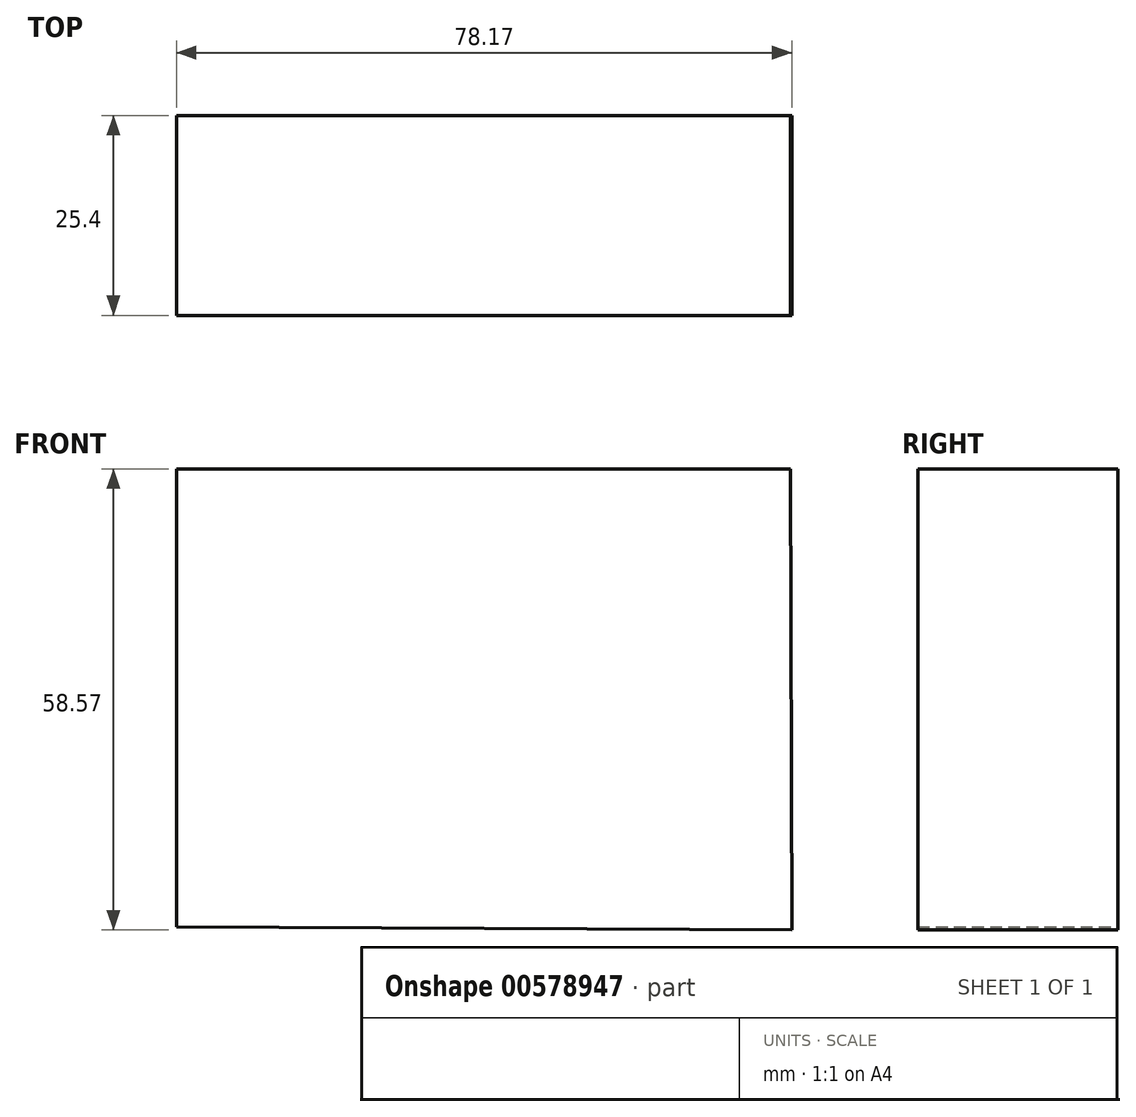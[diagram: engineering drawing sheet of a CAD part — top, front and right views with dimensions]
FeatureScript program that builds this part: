
annotation { "Feature Type Name" : "Feature", "Feature Type Description" : "" }
export const myFeature = defineFeature(function(context is Context, id is Id, definition is map)
    precondition{}
    {
        {
            var Q0;
            Q0=qCreatedBy(makeId("Front.planeOp"),FACE);
            var sketch = newSketch(context, id + "F0", { "sketchPlane" : qUnion([Q0])});
            skLineSegment(sketch, "E0", {"start": v(0, 0) * mm, "end": v(0, 58.18) * mm});
            skLineSegment(sketch, "E1", {"start": v(0, 58.18) * mm, "end": v(78.02, 58.18) * mm});
            skLineSegment(sketch, "E2", {"start": v(78.02, 58.18) * mm, "end": v(78.17, -0.4) * mm});
            skLineSegment(sketch, "E3", {"start": v(78.17, -0.4) * mm, "end": v(0, 0) * mm});
            skSolve(sketch);
        }
        {
            var Q0;
            Q0=makeQuery(id+"F0.imprint","IMPRINT",FACE,{"disambiguationData":[TD([[makeQuery(id+"F0.imprint","IMPRINT",EDGE,{"derivedFrom":sQuery(id+"F0.wireOp",EDGE,"E0")}),-1.0]])]});
            extrude(context, id + "F1", {"entities" : qUnion([Q0]), "depth" : 25.4 * mm, "offsetDistance" : 25.4 * mm});
        }
    });
